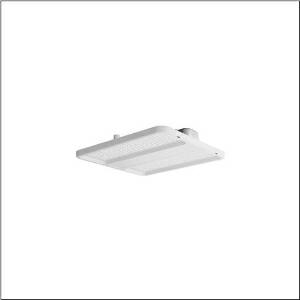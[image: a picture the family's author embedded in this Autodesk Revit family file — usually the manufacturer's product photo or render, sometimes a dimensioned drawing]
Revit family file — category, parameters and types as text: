
# Revit family: highbay_21_midi_52hn12da4nda
name_source: partatom
category: Lighting Fixtures
units: mm (PartAtom-declared; Revit-internal decimal feet)

## family parameters
Cut with Voids When Loaded = No
Host = Face
Light Source = No
Part Type = Normal
Room Calculation Point = No
Round Connector Dimension = Use Diameter
Shared = No

## types (1)
- --- (1 x LED, 5120 lm, 28.2 W, 4000K)
    Apparent Load = 28 VA
    CIE Flux Codes = 90 98 100 100 100
    Color Rendering = 80
    Color Temperature = 4000K
    Default Elevation = 1800 mm
    Description = high bay luminaire Highbay 21 midi; direct symmetric wide distribution, light control with lens of PMMA; UGR ≤ 22 (X = 4H | Y = 8H | S = 0.25H | reflection values 70/50/20); luminous flux: 32.000lm; light colour: 840, colour temperature: 4000K, MacAdam ≤ 3 SDCM (initial), colour rendering: CRI > 80; luminous efficacy: 182lm/W; rated service life: 75.000h (L80/B50) at AT= ta max; control: DALI 2; housing frame of high-performance plastic PA6, matt traffic white (RAL 9016); cover of PMMA; dimension (LxWxH): 474 x 442 x 72mm; luminaire connection: terminal, 5-pole, max. 2.5mm² (cable entry for one cable, Ø 8.5..16mm); mains connection: 230..240V, AC/DC 0/50..60Hz; connected load: 175,8W; protection rating (complete): IP66; insulation class (complete): insulation class I (protective earthing); protection symbol: D; impact resistance: IK08; halogen-free wiring; for central battery installations according to DIN EN 60598-2-22; LABS conformity tested according to VDMA 24364:2018-05; corresponds to IFS (International Featured Standards) requirements for safety and quality in the food industry; certification: CE, ENEC, VDE, UKCA; permissible operating ambient temperature: -40..+50°C (reducing of maximum allowable ambient temperature of 5°C with ceiling mounting); packaging unit: 1 piece; (delivery without accessories; please order mounting accessories separately)
    Height = 72 mm  [stored 0.23622 ft]
    Lamp = 1 x LED
    Lamp Light Flux = 5120 lm
    Lamp Power = 28.2 W
    Lamp count = 1
    Length = 474 mm
    Luminous efficacy = 182 lm/W
    Manufacturer = Siteco
    ModVariant = No
    Model = 52HN12DA4NDA
    Mounting Place = Ceiling
    Mounting Type = Pendant
    Number of Poles = 1
    OnlyDefault = Yes
    Power Factor = 1
    Product Name = Highbay 21 midi
    Product group = high bay luminaire
    ProductGroupID = 901
    Protection Class = Protection class I
    Protection Degree = IP 66
    RLX_Detail_Level = 1
    RLX_Emergency_Light_Flux = 0 lm
    RLX_Emergency_Type = 0
    RLX_Emergency_Type_DB = No
    RlxData = <blob elided: 17669 chars, md5=c9a7ed0a>
    Socket = socket
    Standby Power = 0 W
    System Light Flux = 5120 lm
    System Power = 28 W
    Type Comments = : DC mode (central or group accumulator) initial emergency light level
    Type Image = l_1363240.jpg
    URL = http://relux.com
    VarID = @adj_000563
    Voltage = 0 V
    Weight = 0.00 kg
    Width = 442 mm

note: [stored X ft] marks values corroborated as IEEE doubles in the binary element streams (Revit-internal decimal feet)

## geometry (parser evidence)
native form markers: Blend x4, Sweep x11
no freeform markers — native parametric forms only
